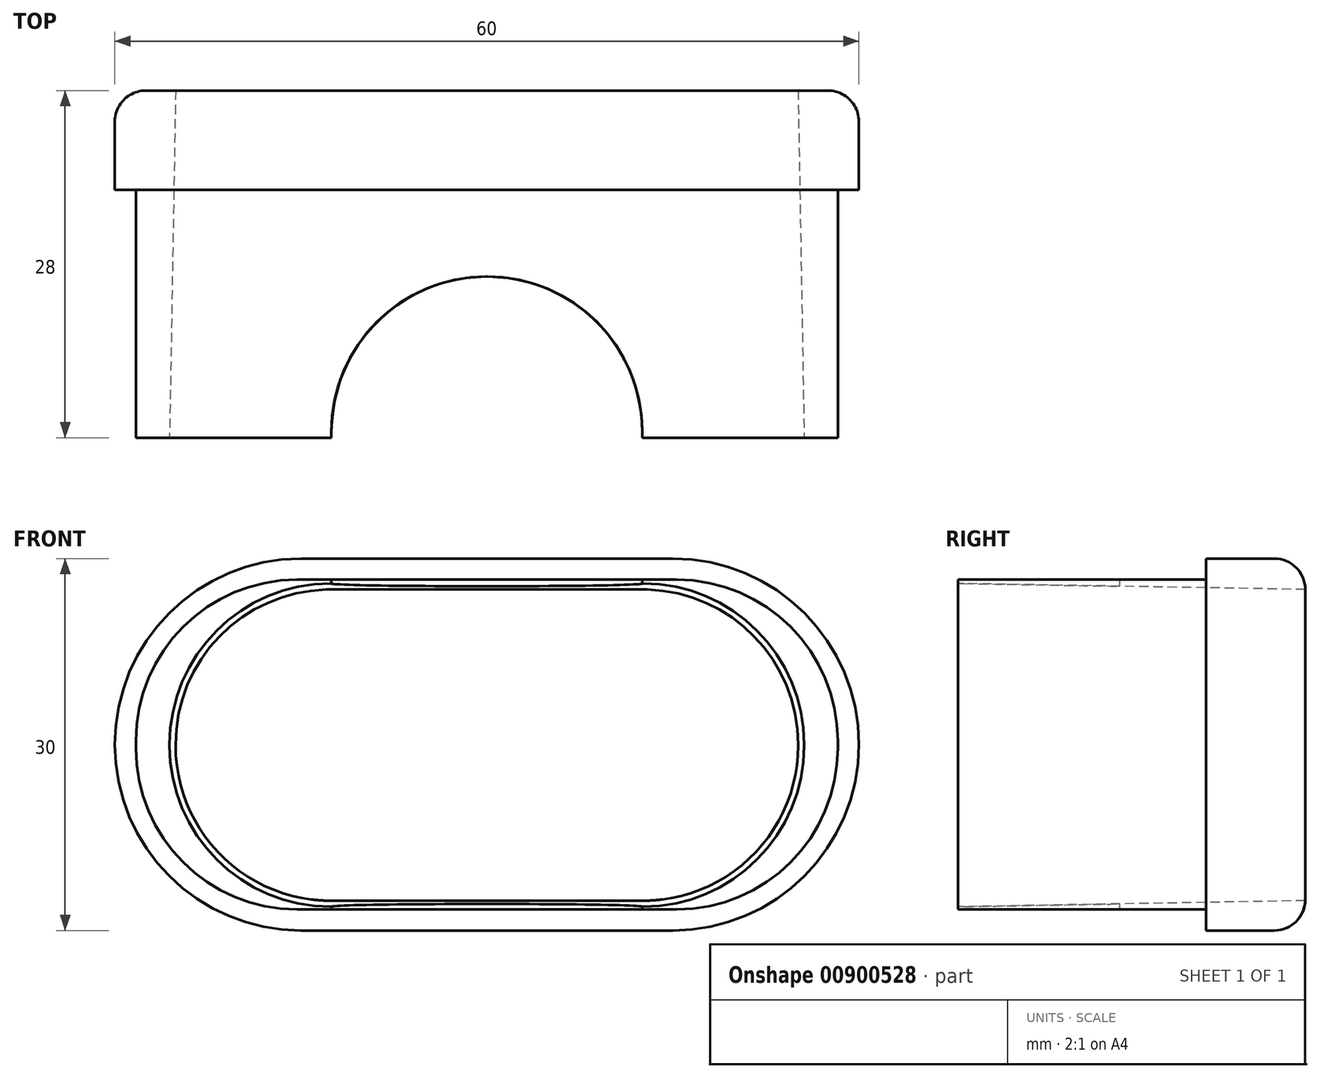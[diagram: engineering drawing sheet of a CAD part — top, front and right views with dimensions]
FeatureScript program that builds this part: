
annotation { "Feature Type Name" : "Feature", "Feature Type Description" : "" }
export const myFeature = defineFeature(function(context is Context, id is Id, definition is map)
    precondition{}
    {
        {
            var Q0;
            Q0=qCreatedBy(makeId("Front.planeOp"),FACE);
            var sketch = newSketch(context, id + "F0", { "sketchPlane" : qUnion([Q0])});
            skLineSegment(sketch, "E0", {"start": v(0, 0) * mm, "end": v(-30, 0) * mm, "construction": true});
            skLineSegment(sketch, "E1", {"start": v(-30, 0) * mm, "end": v(-30, 15) * mm, "construction": true});
            skLineSegment(sketch, "E2", {"start": v(-15, 15) * mm, "end": v(15, 15) * mm});
            skLineSegment(sketch, "E3", {"start": v(30, 0) * mm, "end": v(30, 0) * mm});
            skLineSegment(sketch, "E4", {"start": v(15, -15) * mm, "end": v(-15, -15) * mm});
            skLineSegment(sketch, "E5", {"start": v(-30, 0) * mm, "end": v(-30, 0) * mm});
            skPoint(sketch, "E6.visualSharp", {"position": v(-30, 15) * mm});
            skArc(sketch, "E6.filletArc", {"start": v(-15, 15) * mm, "mid": v(-25.6, 10.6) * mm, "end": v(-30, 0) * mm});
            skPoint(sketch, "E7.visualSharp", {"position": v(-30, -15) * mm});
            skArc(sketch, "E7.filletArc", {"start": v(-30, 0) * mm, "mid": v(-25.6, -10.6) * mm, "end": v(-15, -15) * mm});
            skPoint(sketch, "E8.visualSharp", {"position": v(30, -15) * mm});
            skArc(sketch, "E8.filletArc", {"start": v(15, -15) * mm, "mid": v(25.6, -10.6) * mm, "end": v(30, 0) * mm});
            skPoint(sketch, "E9.visualSharp", {"position": v(30, 15) * mm});
            skArc(sketch, "E9.filletArc", {"start": v(30, 0) * mm, "mid": v(25.6, 10.6) * mm, "end": v(15, 15) * mm});
            skSolve(sketch);
        }
        {
            var Q0;
            Q0=makeQuery(id+"F0.imprint","IMPRINT",FACE,{"disambiguationData":[TD([[makeQuery(id+"F0.imprint","IMPRINT",EDGE,{"derivedFrom":sQuery(id+"F0.wireOp",EDGE,"E2")}),-1.0]])]});
            extrude(context, id + "F1", {"entities" : qUnion([Q0]), "depth" : 8 * mm, "offsetDistance" : 25 * mm});
        }
        {
            var Q0;
            Q0=qCreatedBy(makeId("Front.planeOp"),FACE);
            var sketch = newSketch(context, id + "F2", { "sketchPlane" : qUnion([Q0])});
            skLineSegment(sketch, "E10", {"start": v(0, 0) * mm, "end": v(-25.1, 0) * mm, "construction": true});
            skLineSegment(sketch, "E11", {"start": v(-25.1, 0) * mm, "end": v(-25.1, 0) * mm});
            skLineSegment(sketch, "E12", {"start": v(-12.6, 12.5) * mm, "end": v(12.6, 12.5) * mm});
            skLineSegment(sketch, "E13", {"start": v(25.1, 0) * mm, "end": v(25.1, -0.1) * mm});
            skLineSegment(sketch, "E14", {"start": v(12.6, -12.6) * mm, "end": v(-12.6, -12.6) * mm});
            skLineSegment(sketch, "E15", {"start": v(-25.1, -0.1) * mm, "end": v(-25.1, 0) * mm});
            skPoint(sketch, "E16.visualSharp", {"position": v(-25.1, 12.5) * mm});
            skArc(sketch, "E16.filletArc", {"start": v(-12.6, 12.5) * mm, "mid": v(-21.44, 8.84) * mm, "end": v(-25.1, 0) * mm});
            skPoint(sketch, "E17.visualSharp", {"position": v(-25.1, -12.6) * mm});
            skArc(sketch, "E17.filletArc", {"start": v(-25.1, -0.1) * mm, "mid": v(-21.44, -8.93) * mm, "end": v(-12.6, -12.6) * mm});
            skPoint(sketch, "E18.visualSharp", {"position": v(25.1, -12.6) * mm});
            skArc(sketch, "E18.filletArc", {"start": v(12.6, -12.6) * mm, "mid": v(21.44, -8.93) * mm, "end": v(25.1, -0.1) * mm});
            skPoint(sketch, "E19.visualSharp", {"position": v(25.1, 12.5) * mm});
            skArc(sketch, "E19.filletArc", {"start": v(25.1, 0) * mm, "mid": v(21.44, 8.84) * mm, "end": v(12.6, 12.5) * mm});
            skSolve(sketch);
        }
        {
            var Q0;
            Q0=makeQuery(id+"F1.opExtrude","CAP_EDGE",EDGE,{"disambiguationData":[OSD([sQuery(id+"F0.wireOp",EDGE,"E8.filletArc"),sQuery(id+"F0.wireOp",EDGE,"E9.filletArc")])],"isStart":true});
            fillet(context, id + "F3", {"entities" : qUnion([Q0]), "radius" : 2.5 * mm, "tangentPropagation" : true, "allowEdgeOverflow" : false});
        }
        {
            var Q0;
            Q0=qCreatedBy(makeId("Front.planeOp"),FACE);
            var sketch = newSketch(context, id + "F4", { "sketchPlane" : qUnion([Q0])});
            skLineSegment(sketch, "E20", {"start": v(0, 0) * mm, "end": v(-28.3, 0) * mm, "construction": true});
            skLineSegment(sketch, "E21", {"start": v(-28.3, 0) * mm, "end": v(-28.3, 0.3) * mm});
            skLineSegment(sketch, "E22", {"start": v(-15.3, 13.3) * mm, "end": v(15.3, 13.3) * mm});
            skLineSegment(sketch, "E23", {"start": v(28.3, 0.3) * mm, "end": v(28.3, -0.3) * mm});
            skLineSegment(sketch, "E24", {"start": v(15.3, -13.3) * mm, "end": v(-15.3, -13.3) * mm});
            skLineSegment(sketch, "E25", {"start": v(-28.3, -0.3) * mm, "end": v(-28.3, 0) * mm});
            skPoint(sketch, "E26.visualSharp", {"position": v(-28.3, 13.3) * mm});
            skArc(sketch, "E26.filletArc", {"start": v(-15.3, 13.3) * mm, "mid": v(-24.5, 9.5) * mm, "end": v(-28.3, 0.3) * mm});
            skPoint(sketch, "E27.visualSharp", {"position": v(-28.3, -13.3) * mm});
            skArc(sketch, "E27.filletArc", {"start": v(-28.3, -0.3) * mm, "mid": v(-24.5, -9.5) * mm, "end": v(-15.3, -13.3) * mm});
            skPoint(sketch, "E28.visualSharp", {"position": v(28.3, -13.3) * mm});
            skArc(sketch, "E28.filletArc", {"start": v(15.3, -13.3) * mm, "mid": v(24.5, -9.5) * mm, "end": v(28.3, -0.3) * mm});
            skPoint(sketch, "E29.visualSharp", {"position": v(28.3, 13.3) * mm});
            skArc(sketch, "E29.filletArc", {"start": v(28.3, 0.3) * mm, "mid": v(24.5, 9.5) * mm, "end": v(15.3, 13.3) * mm});
            skSolve(sketch);
        }
        {
            var Q0;
            Q0 = qSketchRegion(id + "F4", true);
            extrude(context, id + "F5", {"entities" : qUnion([Q0]), "operationType" : NewBodyOperationType.ADD, "depth" : 28 * mm, "offsetDistance" : 25 * mm, "hasSecondDirection" : true, "secondDirectionOppositeDirection" : false, "secondDirectionDepth" : 5 * mm});
        }
        {
            var Q0;
            Q0 = qSketchRegion(id + "F2", true);
            extrude(context, id + "F6", {"entities" : qUnion([Q0]), "operationType" : NewBodyOperationType.REMOVE, "depth" : 30 * mm, "offsetDistance" : 25 * mm, "hasDraft" : true, "draftAngle" : 1 * degree});
        }
        {
            var Q0;
            Q0=qCreatedBy(makeId("Front.planeOp"),FACE);
            var sketch = newSketch(context, id + "F7", { "sketchPlane" : qUnion([Q0])});
            skLineSegment(sketch, "E30.bottom", {"start": v(-12.53, 16.79) * mm, "end": v(12.53, 16.79) * mm});
            skLineSegment(sketch, "E30.top", {"start": v(-12.53, -16.79) * mm, "end": v(12.53, -16.79) * mm});
            skLineSegment(sketch, "E30.left", {"start": v(-12.53, 16.79) * mm, "end": v(-12.53, -16.79) * mm});
            skLineSegment(sketch, "E30.right", {"start": v(12.53, 16.79) * mm, "end": v(12.53, -16.79) * mm});
            skPoint(sketch, "E30.middle", {"position": v(0, 0) * mm});
            skSolve(sketch);
        }
        {
            var Q0;
            Q0=makeQuery(id+"F7.imprint","IMPRINT",FACE,{"disambiguationData":[TD([[makeQuery(id+"F7.imprint","IMPRINT",EDGE,{"derivedFrom":sQuery(id+"F7.wireOp",EDGE,"E30.bottom")}),-1.0]])]});
            extrude(context, id + "F8", {"entities" : qUnion([Q0]), "operationType" : NewBodyOperationType.REMOVE, "depth" : 30 * mm, "offsetDistance" : 25 * mm, "hasSecondDirection" : true, "secondDirectionOppositeDirection" : false, "secondDirectionDepth" : 15 * mm});
        }
        {
            var Q0;
            {var subQ0=sQuery(id+"F7.wireOp",EDGE,"E30.right");Q0=makeQuery(id+"F8.boolean.opBoolean","COPY",EDGE,{"disambiguationData":[TD([makeQuery(id+"F5.opExtrude","SWEPT_FACE",FACE,{"disambiguationData":[OSD([sQuery(id+"F4.wireOp",EDGE,"E22")])]})])],"derivedFrom":makeQuery(id+"F8.opExtrude","CAP_EDGE",EDGE,{"disambiguationData":[OSD([subQ0])],"isStart":true})});}
            var Q1;
            {var subQ0=sQuery(id+"F7.wireOp",EDGE,"E30.left");Q1=makeQuery(id+"F8.boolean.opBoolean","COPY",EDGE,{"disambiguationData":[TD([makeQuery(id+"F5.opExtrude","SWEPT_FACE",FACE,{"disambiguationData":[OSD([sQuery(id+"F4.wireOp",EDGE,"E22")])]})])],"derivedFrom":makeQuery(id+"F8.opExtrude","CAP_EDGE",EDGE,{"disambiguationData":[OSD([subQ0])],"isStart":true})});}
            var Q2;
            {var subQ0=sQuery(id+"F7.wireOp",EDGE,"E30.left");Q2=makeQuery(id+"F8.boolean.opBoolean","COPY",EDGE,{"disambiguationData":[TD([makeQuery(id+"F5.opExtrude","SWEPT_FACE",FACE,{"disambiguationData":[OSD([sQuery(id+"F4.wireOp",EDGE,"E24")])]})])],"derivedFrom":makeQuery(id+"F8.opExtrude","CAP_EDGE",EDGE,{"disambiguationData":[OSD([subQ0])],"isStart":true})});}
            var Q3;
            {var subQ0=sQuery(id+"F7.wireOp",EDGE,"E30.right");Q3=makeQuery(id+"F8.boolean.opBoolean","COPY",EDGE,{"disambiguationData":[TD([makeQuery(id+"F5.opExtrude","SWEPT_FACE",FACE,{"disambiguationData":[OSD([sQuery(id+"F4.wireOp",EDGE,"E24")])]})])],"derivedFrom":makeQuery(id+"F8.opExtrude","CAP_EDGE",EDGE,{"disambiguationData":[OSD([subQ0])],"isStart":true})});}
            fillet(context, id + "F9", {"entities" : qUnion([Q0, Q1, Q2, Q3]), "radius" : 12.5 * mm, "tangentPropagation" : true, "allowEdgeOverflow" : false});
        }
    });
